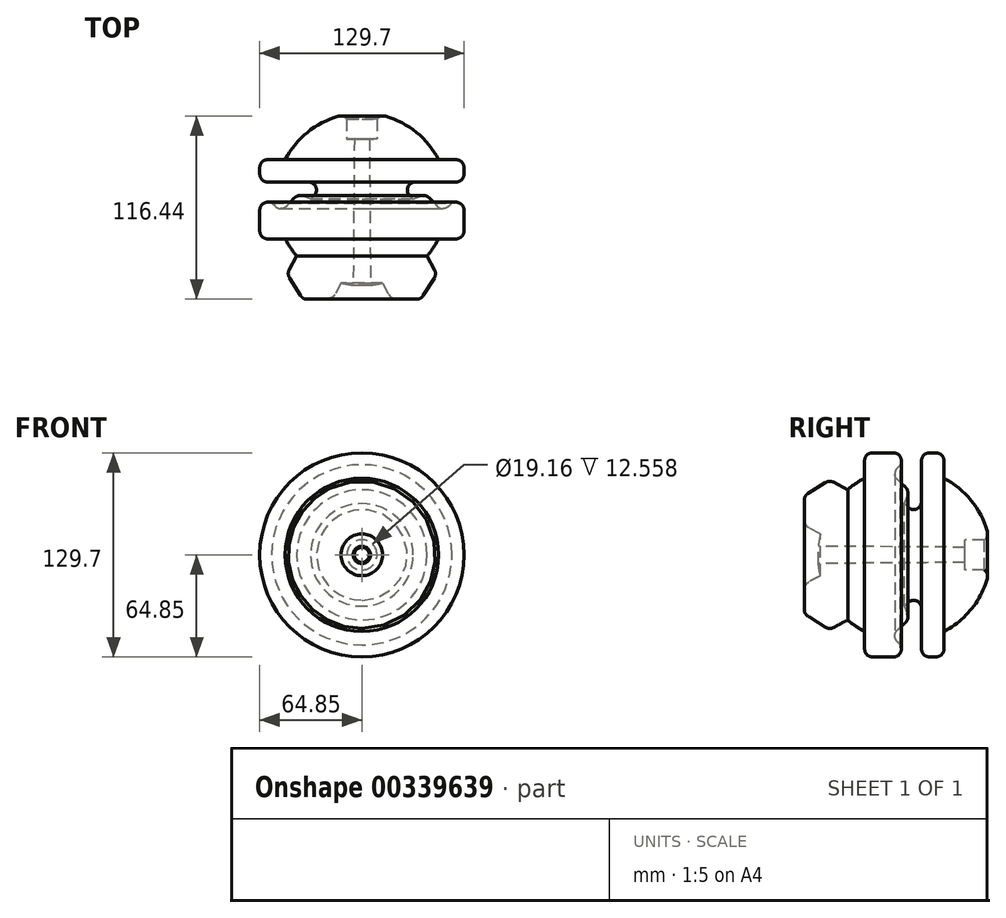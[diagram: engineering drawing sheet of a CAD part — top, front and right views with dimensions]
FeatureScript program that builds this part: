
annotation { "Feature Type Name" : "Feature", "Feature Type Description" : "" }
export const myFeature = defineFeature(function(context is Context, id is Id, definition is map)
    precondition{}
    {
        {
            var Q0;
            Q0=qCreatedBy(makeId("Top.planeOp"),FACE);
            var sketch = newSketch(context, id + "F0", { "sketchPlane" : qUnion([Q0])});
            skArc(sketch, "E0", {"start": v(-48.68, -25.16) * mm, "mid": v(-45.24, -30.92) * mm, "end": v(-41.12, -36.22) * mm});
            skLineSegment(sketch, "E1.right", {"start": v(-64.85, 20.16) * mm, "end": v(-64.85, 15.97) * mm});
            skLineSegment(sketch, "E2.trimOffspring", {"start": v(-48.68, 25.16) * mm, "end": v(-59.85, 25.16) * mm});
            skLineSegment(sketch, "E3.trimOffspring", {"start": v(-48.68, -25.16) * mm, "end": v(-59.85, -25.16) * mm});
            skPoint(sketch, "E4.endSnap0", {"position": v(0, 54.8) * mm});
            skLineSegment(sketch, "E5", {"start": v(0, -49.55) * mm, "end": v(0, 38.4) * mm});
            skArc(sketch, "E6.trimOffspring", {"start": v(-14.92, 52.73) * mm, "mid": v(-34.66, 42.45) * mm, "end": v(-48.68, 25.16) * mm});
            skPoint(sketch, "E1.left.start.orphan", {"position": v(64.85, 25.16) * mm});
            skPoint(sketch, "E1.top.start.orphan", {"position": v(64.85, -25.16) * mm});
            skArc(sketch, "E7.cCircle", {"start": v(-41.12, -36.22) * mm, "mid": v(-37.07, -60.89) * mm, "end": v(-13.29, -53.16) * mm, "construction": true});
            skLineSegment(sketch, "E7.1", {"start": v(-13.22, -53.18) * mm, "end": v(-17.05, -60.4) * mm});
            skLineSegment(sketch, "E7.2", {"start": v(-21.29, -63.05) * mm, "end": v(-34.54, -63.51) * mm});
            skLineSegment(sketch, "E7.3", {"start": v(-38.96, -61.17) * mm, "end": v(-45.99, -49.92) * mm});
            skLineSegment(sketch, "E7.4", {"start": v(-46.16, -44.93) * mm, "end": v(-41.38, -35.93) * mm});
            skPoint(sketch, "E7.0.midPoint", {"position": v(-14.52, -38.07) * mm});
            skArc(sketch, "E8.trimOffspring", {"start": v(-13.29, -53.16) * mm, "mid": v(-9.42, -53.98) * mm, "end": v(-5.5, -54.52) * mm});
            skPoint(sketch, "E9.orphan", {"position": v(-19.56, -30) * mm});
            skPoint(sketch, "E10.orphan", {"position": v(-9.47, -46.14) * mm});
            skLineSegment(sketch, "E11", {"start": v(-59.85, 10.97) * mm, "end": v(-33.83, 10.97) * mm});
            skLineSegment(sketch, "E12", {"start": v(-30.2, 2.54) * mm, "end": v(-32.58, 0) * mm});
            skLineSegment(sketch, "E13", {"start": v(-32.58, 0) * mm, "end": v(-37.5, 1.96) * mm});
            skLineSegment(sketch, "E14", {"start": v(-42.99, 0.75) * mm, "end": v(-47.87, -4.43) * mm});
            skLineSegment(sketch, "E15", {"start": v(-54.93, -4.64) * mm, "end": v(-57.24, -2.46) * mm});
            skLineSegment(sketch, "E16", {"start": v(-57.24, -2.46) * mm, "end": v(-58.3, -2.12) * mm});
            skLineSegment(sketch, "E17.trimOffspring", {"start": v(-64.85, -6.87) * mm, "end": v(-64.85, -20.16) * mm});
            skPoint(sketch, "E18.visualSharp", {"position": v(-64.85, 25.16) * mm});
            skArc(sketch, "E18.filletArc", {"start": v(-59.85, 25.16) * mm, "mid": v(-63.38, 23.7) * mm, "end": v(-64.85, 20.16) * mm});
            skPoint(sketch, "E19.visualSharp", {"position": v(-64.85, -25.16) * mm});
            skArc(sketch, "E19.filletArc", {"start": v(-64.85, -20.16) * mm, "mid": v(-63.38, -23.7) * mm, "end": v(-59.85, -25.16) * mm});
            skPoint(sketch, "E20.visualSharp", {"position": v(-64.85, 0) * mm});
            skArc(sketch, "E20.filletArc", {"start": v(-58.3, -2.12) * mm, "mid": v(-62.79, -2.83) * mm, "end": v(-64.85, -6.87) * mm});
            skPoint(sketch, "E21.visualSharp", {"position": v(-64.85, 10.97) * mm});
            skArc(sketch, "E21.filletArc", {"start": v(-64.85, 15.97) * mm, "mid": v(-63.38, 12.43) * mm, "end": v(-59.85, 10.97) * mm});
            skPoint(sketch, "E22.visualSharp", {"position": v(-47.52, -47.48) * mm});
            skArc(sketch, "E22.filletArc", {"start": v(-46.16, -44.93) * mm, "mid": v(-46.74, -47.45) * mm, "end": v(-45.99, -49.92) * mm});
            skPoint(sketch, "E23.visualSharp", {"position": v(-18.4, -62.95) * mm});
            skArc(sketch, "E23.filletArc", {"start": v(-21.29, -63.05) * mm, "mid": v(-18.82, -62.29) * mm, "end": v(-17.05, -60.4) * mm});
            skPoint(sketch, "E24.visualSharp", {"position": v(0, -54.8) * mm});
            skPoint(sketch, "E25.visualSharp", {"position": v(-11.57, 53.56) * mm});
            skArc(sketch, "E25.filletArc", {"start": v(-9.58, 50.95) * mm, "mid": v(-11.97, 52.66) * mm, "end": v(-14.92, 52.73) * mm});
            skLineSegment(sketch, "E26", {"start": v(-9.58, 50.95) * mm, "end": v(-9.58, 38.4) * mm});
            skLineSegment(sketch, "E27", {"start": v(-9.58, 38.4) * mm, "end": v(-4.8, 38.4) * mm});
            skLineSegment(sketch, "E28", {"start": v(-4.8, 38.4) * mm, "end": v(-5.5, -54.52) * mm});
            skPoint(sketch, "E29.visualSharp", {"position": v(-40.65, 3.23) * mm});
            skArc(sketch, "E29.filletArc", {"start": v(-37.5, 1.96) * mm, "mid": v(-40.42, 2.2) * mm, "end": v(-42.99, 0.75) * mm});
            skPoint(sketch, "E30.visualSharp", {"position": v(-22.26, 10.97) * mm});
            skArc(sketch, "E30.filletArc", {"start": v(-30.2, 2.54) * mm, "mid": v(-29.24, 7.95) * mm, "end": v(-33.83, 10.97) * mm});
            skPoint(sketch, "E31.visualSharp", {"position": v(-51.3, -8.07) * mm});
            skArc(sketch, "E31.filletArc", {"start": v(-54.93, -4.64) * mm, "mid": v(-51.36, -6) * mm, "end": v(-47.87, -4.43) * mm});
            skPoint(sketch, "E32.visualSharp", {"position": v(-37.43, -63.61) * mm});
            skArc(sketch, "E32.filletArc", {"start": v(-38.96, -61.17) * mm, "mid": v(-37.06, -62.93) * mm, "end": v(-34.54, -63.51) * mm});
            skSolve(sketch);
        }
        {
            var Q0;
            Q0 = qSketchRegion(id + "F0", true);
            var Q1;
            Q1=sQuery(id+"F0.wireOp",EDGE,"E5");
            revolve(context, id + "F1", {"entities" : qUnion([Q0]), "axis" : qUnion([Q1]), "revolveType" : RevolveType.FULL});
        }
    });
